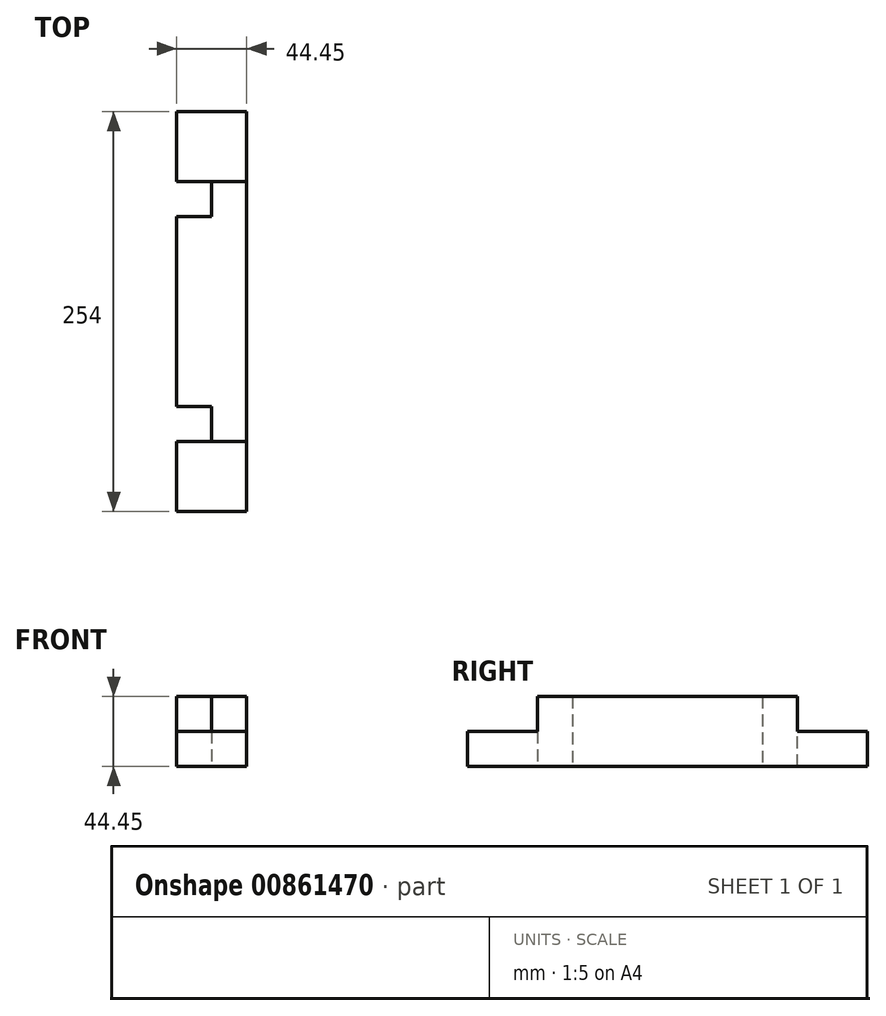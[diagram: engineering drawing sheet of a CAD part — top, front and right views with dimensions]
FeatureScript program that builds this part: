
annotation { "Feature Type Name" : "Feature", "Feature Type Description" : "" }
export const myFeature = defineFeature(function(context is Context, id is Id, definition is map)
    precondition{}
    {
        {
            var Q0;
            Q0=qCreatedBy(makeId("Front.planeOp"),FACE);
            var sketch = newSketch(context, id + "F0", { "sketchPlane" : qUnion([Q0])});
            skLineSegment(sketch, "E0.bottom", {"start": v(0, 0) * mm, "end": v(44.45, 0) * mm});
            skLineSegment(sketch, "E0.top", {"start": v(0, 44.45) * mm, "end": v(44.45, 44.45) * mm});
            skLineSegment(sketch, "E0.left", {"start": v(0, 0) * mm, "end": v(0, 44.45) * mm});
            skLineSegment(sketch, "E0.right", {"start": v(44.45, 0) * mm, "end": v(44.45, 44.45) * mm});
            skSolve(sketch);
        }
        {
            var Q0;
            Q0=makeQuery(id+"F0.imprint","IMPRINT",FACE,{"disambiguationData":[TD([[makeQuery(id+"F0.imprint","IMPRINT",EDGE,{"derivedFrom":sQuery(id+"F0.wireOp",EDGE,"E0.bottom")}),1.0]])]});
            extrude(context, id + "F1", {"entities" : qUnion([Q0]), "depth" : 254 * mm, "offsetDistance" : 25.4 * mm});
        }
        {
            var Q0;
            Q0=makeQuery(id+"F1.opExtrude","SWEPT_FACE",FACE,{"disambiguationData":[OSD([sQuery(id+"F0.wireOp",EDGE,"E0.top")])]});
            var sketch = newSketch(context, id + "F2", { "sketchPlane" : qUnion([Q0])});
            skLineSegment(sketch, "E1.bottom", {"start": v(0, -254) * mm, "end": v(44.45, -254) * mm});
            skLineSegment(sketch, "E1.top", {"start": v(0, -209.55) * mm, "end": v(44.45, -209.55) * mm});
            skLineSegment(sketch, "E1.left", {"start": v(0, -254) * mm, "end": v(0, -209.55) * mm});
            skLineSegment(sketch, "E1.right", {"start": v(44.45, -254) * mm, "end": v(44.45, -209.55) * mm});
            skLineSegment(sketch, "E2.bottom", {"start": v(0, 0) * mm, "end": v(44.45, 0) * mm});
            skLineSegment(sketch, "E2.top", {"start": v(0, -44.45) * mm, "end": v(44.45, -44.45) * mm});
            skLineSegment(sketch, "E2.left", {"start": v(0, 0) * mm, "end": v(0, -44.45) * mm});
            skLineSegment(sketch, "E2.right", {"start": v(44.45, 0) * mm, "end": v(44.45, -44.45) * mm});
            skSolve(sketch);
        }
        {
            var Q0;
            Q0=qSketchRegion(id+"F2",true);
            extrude(context, id + "F3", {"entities" : qUnion([Q0]), "operationType" : NewBodyOperationType.REMOVE, "oppositeDirection" : true, "depth" : 22.22 * mm, "offsetDistance" : 25.4 * mm});
        }
        {
            var Q0;
            Q0=makeQuery(id+"F1.opExtrude","SWEPT_FACE",FACE,{"disambiguationData":[OSD([sQuery(id+"F0.wireOp",EDGE,"E0.left")])]});
            var sketch = newSketch(context, id + "F4", { "sketchPlane" : qUnion([Q0])});
            skLineSegment(sketch, "E3.bottom", {"start": v(44.45, 44.45) * mm, "end": v(66.67, 44.45) * mm});
            skLineSegment(sketch, "E3.top", {"start": v(44.45, 0) * mm, "end": v(66.67, 0) * mm});
            skLineSegment(sketch, "E3.left", {"start": v(44.45, 44.45) * mm, "end": v(44.45, 0) * mm});
            skLineSegment(sketch, "E3.right", {"start": v(66.67, 44.45) * mm, "end": v(66.67, 0) * mm});
            skLineSegment(sketch, "E4.bottom", {"start": v(209.55, 44.45) * mm, "end": v(187.33, 44.45) * mm});
            skLineSegment(sketch, "E4.top", {"start": v(209.55, 0) * mm, "end": v(187.33, 0) * mm});
            skLineSegment(sketch, "E4.left", {"start": v(209.55, 44.45) * mm, "end": v(209.55, 0) * mm});
            skLineSegment(sketch, "E4.right", {"start": v(187.33, 44.45) * mm, "end": v(187.33, 0) * mm});
            skSolve(sketch);
        }
        {
            var Q0;
            Q0 = qSketchRegion(id + "F4", true);
            extrude(context, id + "F5", {"entities" : qUnion([Q0]), "operationType" : NewBodyOperationType.REMOVE, "oppositeDirection" : true, "depth" : 22.22 * mm, "offsetDistance" : 25.4 * mm});
        }
    });
